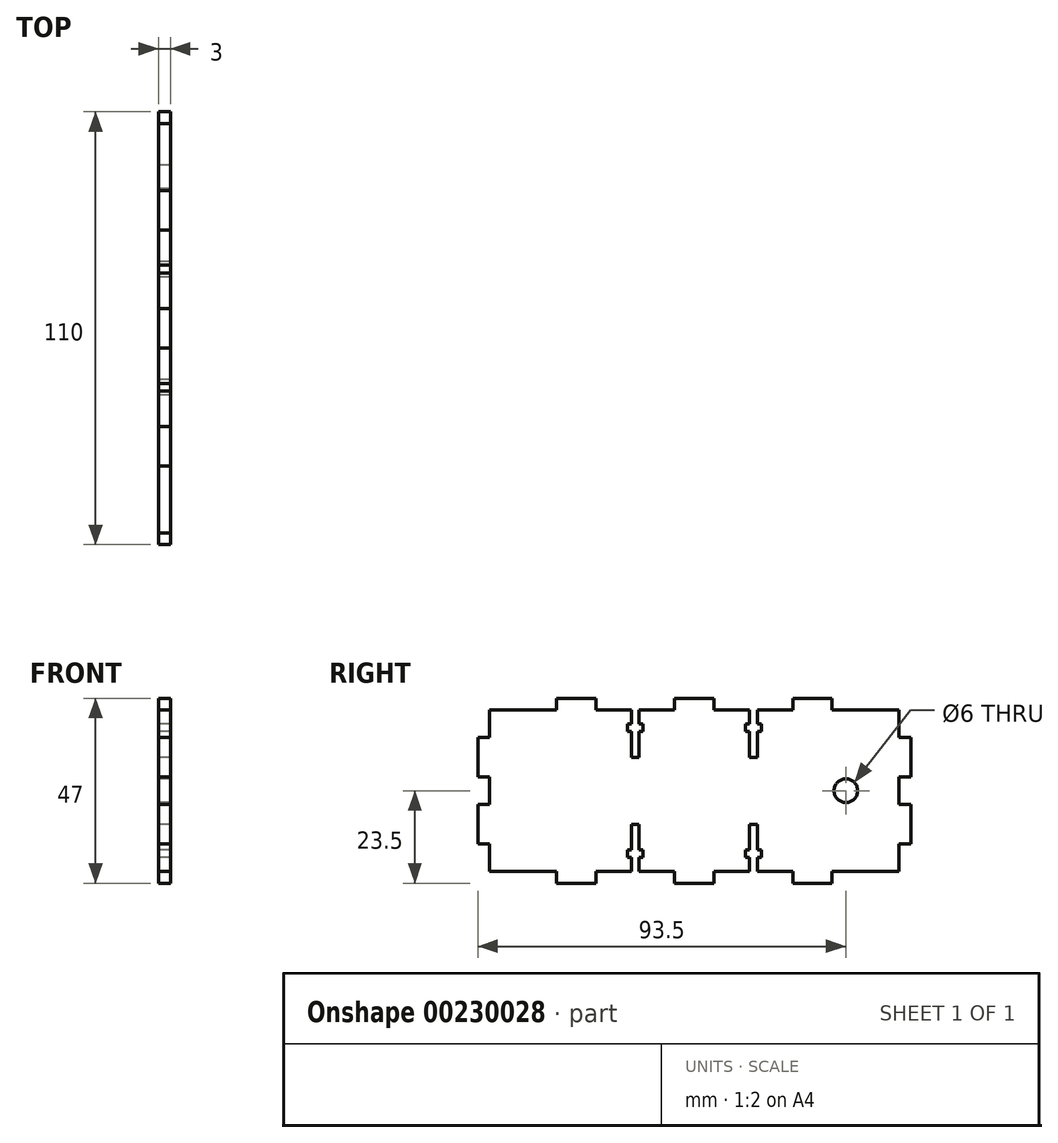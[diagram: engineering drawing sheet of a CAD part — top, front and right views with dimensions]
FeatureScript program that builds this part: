
annotation { "Feature Type Name" : "Feature", "Feature Type Description" : "" }
export const myFeature = defineFeature(function(context is Context, id is Id, definition is map)
    precondition{}
    {
        {
            var Q0;
            Q0=qCreatedBy(makeId("Right.planeOp"),FACE);
            var sketch = newSketch(context, id + "F0", { "sketchPlane" : qUnion([Q0])});
            skLineSegment(sketch, "E0", {"start": v(0, 0) * mm, "end": v(0, 7) * mm});
            skLineSegment(sketch, "E1", {"start": v(0, 7) * mm, "end": v(-3, 7) * mm});
            skLineSegment(sketch, "E2", {"start": v(-3, 7) * mm, "end": v(-3, 17) * mm});
            skLineSegment(sketch, "E3", {"start": v(-3, 17) * mm, "end": v(0, 17) * mm});
            skLineSegment(sketch, "E4", {"start": v(0, 17) * mm, "end": v(0, 20.5) * mm});
            skLineSegment(sketch, "E5", {"start": v(0, 0) * mm, "end": v(17, 0) * mm});
            skLineSegment(sketch, "E6", {"start": v(17, 0) * mm, "end": v(17, -3) * mm});
            skLineSegment(sketch, "E7", {"start": v(17, -3) * mm, "end": v(27, -3) * mm});
            skLineSegment(sketch, "E8", {"start": v(27, 0) * mm, "end": v(27, -3) * mm});
            skLineSegment(sketch, "E9", {"start": v(27, 0) * mm, "end": v(36, 0) * mm});
            skLineSegment(sketch, "E10", {"start": v(36, 0) * mm, "end": v(36, 3.5) * mm});
            skLineSegment(sketch, "E11", {"start": v(36, 3.5) * mm, "end": v(35, 3.5) * mm});
            skLineSegment(sketch, "E12", {"start": v(35, 3.5) * mm, "end": v(35, 5.5) * mm});
            skLineSegment(sketch, "E13", {"start": v(35, 5.5) * mm, "end": v(36, 5.5) * mm});
            skLineSegment(sketch, "E14", {"start": v(36, 5.5) * mm, "end": v(36, 12) * mm});
            skLineSegment(sketch, "E15", {"start": v(36, 12) * mm, "end": v(38, 12) * mm});
            skLineSegment(sketch, "E16", {"start": v(38, 12) * mm, "end": v(38, 5.5) * mm});
            skLineSegment(sketch, "E17", {"start": v(38, 5.5) * mm, "end": v(39, 5.5) * mm});
            skLineSegment(sketch, "E18", {"start": v(38, 3.5) * mm, "end": v(39, 3.5) * mm});
            skLineSegment(sketch, "E19", {"start": v(38, 0) * mm, "end": v(38, 3.5) * mm});
            skLineSegment(sketch, "E20", {"start": v(38, 0) * mm, "end": v(47, 0) * mm});
            skLineSegment(sketch, "E21", {"start": v(39, 3.5) * mm, "end": v(39, 5.5) * mm});
            skLineSegment(sketch, "E22", {"start": v(47, 0) * mm, "end": v(47, -3) * mm});
            skLineSegment(sketch, "E23", {"start": v(47, -3) * mm, "end": v(52, -3) * mm});
            skLineSegment(sketch, "E24", {"start": v(0, 20.5) * mm, "end": v(52, 20.5) * mm, "construction": true});
            skLineSegment(sketch, "E25", {"start": v(52, 20.5) * mm, "end": v(52, -3) * mm, "construction": true});
            skLineSegment(sketch, "E26.MirrorCS", {"start": v(35, 35.5) * mm, "end": v(36, 35.5) * mm});
            skLineSegment(sketch, "E27.MirrorCS", {"start": v(39, 37.5) * mm, "end": v(39, 35.5) * mm});
            skLineSegment(sketch, "E28.MirrorCS", {"start": v(36, 37.5) * mm, "end": v(35, 37.5) * mm});
            skLineSegment(sketch, "E29.MirrorCS", {"start": v(35, 37.5) * mm, "end": v(35, 35.5) * mm});
            skLineSegment(sketch, "E30.MirrorCS", {"start": v(38, 35.5) * mm, "end": v(39, 35.5) * mm});
            skLineSegment(sketch, "E31.MirrorCS", {"start": v(38, 37.5) * mm, "end": v(39, 37.5) * mm});
            skLineSegment(sketch, "E32.MirrorCS", {"start": v(36, 29) * mm, "end": v(38, 29) * mm});
            skLineSegment(sketch, "E33.MirrorCS", {"start": v(36, 41) * mm, "end": v(36, 37.5) * mm});
            skLineSegment(sketch, "E34.MirrorCS", {"start": v(27, 41) * mm, "end": v(27, 44) * mm});
            skLineSegment(sketch, "E35.MirrorCS", {"start": v(0, 34) * mm, "end": v(-3, 34) * mm});
            skLineSegment(sketch, "E36.MirrorCS", {"start": v(36, 35.5) * mm, "end": v(36, 29) * mm});
            skLineSegment(sketch, "E37.MirrorCS", {"start": v(38, 41) * mm, "end": v(38, 37.5) * mm});
            skLineSegment(sketch, "E38.MirrorCS", {"start": v(27, 41) * mm, "end": v(36, 41) * mm});
            skLineSegment(sketch, "E39.MirrorCS", {"start": v(38, 29) * mm, "end": v(38, 35.5) * mm});
            skLineSegment(sketch, "E40.MirrorCS", {"start": v(38, 41) * mm, "end": v(47, 41) * mm});
            skLineSegment(sketch, "E41.MirrorCS", {"start": v(0, 41) * mm, "end": v(17, 41) * mm});
            skLineSegment(sketch, "E42.MirrorCS", {"start": v(17, 41) * mm, "end": v(17, 44) * mm});
            skLineSegment(sketch, "E43.MirrorCS", {"start": v(-3, 34) * mm, "end": v(-3, 24) * mm});
            skLineSegment(sketch, "E44.MirrorCS", {"start": v(-3, 24) * mm, "end": v(0, 24) * mm});
            skLineSegment(sketch, "E45.MirrorCS", {"start": v(0, 41) * mm, "end": v(0, 34) * mm});
            skLineSegment(sketch, "E46.MirrorCS", {"start": v(47, 41) * mm, "end": v(47, 44) * mm});
            skLineSegment(sketch, "E47.MirrorCS", {"start": v(17, 44) * mm, "end": v(27, 44) * mm});
            skLineSegment(sketch, "E48.MirrorCS", {"start": v(0, 24) * mm, "end": v(0, 20.5) * mm});
            skLineSegment(sketch, "E49.MirrorCS", {"start": v(47, 44) * mm, "end": v(52, 44) * mm});
            skLineSegment(sketch, "E50.MirrorCS", {"start": v(52, 20.5) * mm, "end": v(52, 44) * mm, "construction": true});
            skLineSegment(sketch, "E51.MirrorCS", {"start": v(69, 37.5) * mm, "end": v(69, 35.5) * mm});
            skLineSegment(sketch, "E52.MirrorCS", {"start": v(69, 35.5) * mm, "end": v(68, 35.5) * mm});
            skLineSegment(sketch, "E53.MirrorCS", {"start": v(68, 29) * mm, "end": v(66, 29) * mm});
            skLineSegment(sketch, "E54.MirrorCS", {"start": v(66, 37.5) * mm, "end": v(65, 37.5) * mm});
            skLineSegment(sketch, "E55.MirrorCS", {"start": v(66, 3.5) * mm, "end": v(65, 3.5) * mm});
            skLineSegment(sketch, "E56.MirrorCS", {"start": v(68, 3.5) * mm, "end": v(69, 3.5) * mm});
            skLineSegment(sketch, "E57.MirrorCS", {"start": v(69, 3.5) * mm, "end": v(69, 5.5) * mm});
            skLineSegment(sketch, "E58.MirrorCS", {"start": v(66, 5.5) * mm, "end": v(65, 5.5) * mm});
            skLineSegment(sketch, "E59.MirrorCS", {"start": v(65, 37.5) * mm, "end": v(65, 35.5) * mm});
            skLineSegment(sketch, "E60.MirrorCS", {"start": v(66, 35.5) * mm, "end": v(65, 35.5) * mm});
            skLineSegment(sketch, "E61.MirrorCS", {"start": v(69, 5.5) * mm, "end": v(68, 5.5) * mm});
            skLineSegment(sketch, "E62.MirrorCS", {"start": v(65, 3.5) * mm, "end": v(65, 5.5) * mm});
            skLineSegment(sketch, "E63.MirrorCS", {"start": v(68, 37.5) * mm, "end": v(69, 37.5) * mm});
            skLineSegment(sketch, "E64.MirrorCS", {"start": v(68, 12) * mm, "end": v(66, 12) * mm});
            skLineSegment(sketch, "E65.MirrorCS", {"start": v(77, 41) * mm, "end": v(77, 44) * mm});
            skLineSegment(sketch, "E66.MirrorCS", {"start": v(66, 0) * mm, "end": v(57, 0) * mm});
            skLineSegment(sketch, "E67.MirrorCS", {"start": v(104, 41) * mm, "end": v(104, 34) * mm});
            skLineSegment(sketch, "E68.MirrorCS", {"start": v(87, 41) * mm, "end": v(87, 44) * mm});
            skLineSegment(sketch, "E69.MirrorCS", {"start": v(66, 0) * mm, "end": v(66, 3.5) * mm});
            skLineSegment(sketch, "E70.MirrorCS", {"start": v(66, 12) * mm, "end": v(66, 5.5) * mm});
            skLineSegment(sketch, "E71.MirrorCS", {"start": v(68, 35.5) * mm, "end": v(68, 29) * mm});
            skLineSegment(sketch, "E72.MirrorCS", {"start": v(104, 24) * mm, "end": v(104, 20.5) * mm});
            skLineSegment(sketch, "E73.MirrorCS", {"start": v(104, 34) * mm, "end": v(107, 34) * mm});
            skLineSegment(sketch, "E74.MirrorCS", {"start": v(87, 44) * mm, "end": v(77, 44) * mm});
            skLineSegment(sketch, "E75.MirrorCS", {"start": v(68, 0) * mm, "end": v(68, 3.5) * mm});
            skLineSegment(sketch, "E76.MirrorCS", {"start": v(68, 41) * mm, "end": v(68, 37.5) * mm});
            skLineSegment(sketch, "E77.MirrorCS", {"start": v(87, 0) * mm, "end": v(87, -3) * mm});
            skLineSegment(sketch, "E78.MirrorCS", {"start": v(104, 0) * mm, "end": v(104, 7) * mm});
            skLineSegment(sketch, "E79.MirrorCS", {"start": v(57, 44) * mm, "end": v(52, 44) * mm});
            skLineSegment(sketch, "E80.MirrorCS", {"start": v(77, 0) * mm, "end": v(68, 0) * mm});
            skLineSegment(sketch, "E81.MirrorCS", {"start": v(57, 0) * mm, "end": v(57, -3) * mm});
            skLineSegment(sketch, "E82.MirrorCS", {"start": v(104, 7) * mm, "end": v(107, 7) * mm});
            skLineSegment(sketch, "E83.MirrorCS", {"start": v(77, 41) * mm, "end": v(68, 41) * mm});
            skLineSegment(sketch, "E84.MirrorCS", {"start": v(107, 34) * mm, "end": v(107, 24) * mm});
            skLineSegment(sketch, "E85.MirrorCS", {"start": v(107, 7) * mm, "end": v(107, 17) * mm});
            skLineSegment(sketch, "E86.MirrorCS", {"start": v(66, 29) * mm, "end": v(66, 35.5) * mm});
            skLineSegment(sketch, "E87.MirrorCS", {"start": v(57, -3) * mm, "end": v(52, -3) * mm});
            skLineSegment(sketch, "E88.MirrorCS", {"start": v(66, 41) * mm, "end": v(66, 37.5) * mm});
            skLineSegment(sketch, "E89.MirrorCS", {"start": v(57, 41) * mm, "end": v(57, 44) * mm});
            skLineSegment(sketch, "E90.MirrorCS", {"start": v(66, 41) * mm, "end": v(57, 41) * mm});
            skLineSegment(sketch, "E91.MirrorCS", {"start": v(104, 20.5) * mm, "end": v(52, 20.5) * mm, "construction": true});
            skLineSegment(sketch, "E92.MirrorCS", {"start": v(107, 24) * mm, "end": v(104, 24) * mm});
            skLineSegment(sketch, "E93.MirrorCS", {"start": v(104, 0) * mm, "end": v(87, 0) * mm});
            skLineSegment(sketch, "E94.MirrorCS", {"start": v(87, -3) * mm, "end": v(77, -3) * mm});
            skLineSegment(sketch, "E95.MirrorCS", {"start": v(68, 5.5) * mm, "end": v(68, 12) * mm});
            skLineSegment(sketch, "E96.MirrorCS", {"start": v(77, 0) * mm, "end": v(77, -3) * mm});
            skLineSegment(sketch, "E97.MirrorCS", {"start": v(104, 41) * mm, "end": v(87, 41) * mm});
            skLineSegment(sketch, "E98.MirrorCS", {"start": v(104, 17) * mm, "end": v(104, 20.5) * mm});
            skLineSegment(sketch, "E99.MirrorCS", {"start": v(107, 17) * mm, "end": v(104, 17) * mm});
            skCircle(sketch, "E100", {"center": v(90.5, 20.5) * mm, "radius": 3 * mm});
            skSolve(sketch);
        }
        {
            var Q0;
            Q0 = qSketchRegion(id + "F0", true);
            extrude(context, id + "F1", {"entities" : qUnion([Q0]), "depth" : 3 * mm});
        }
    });
